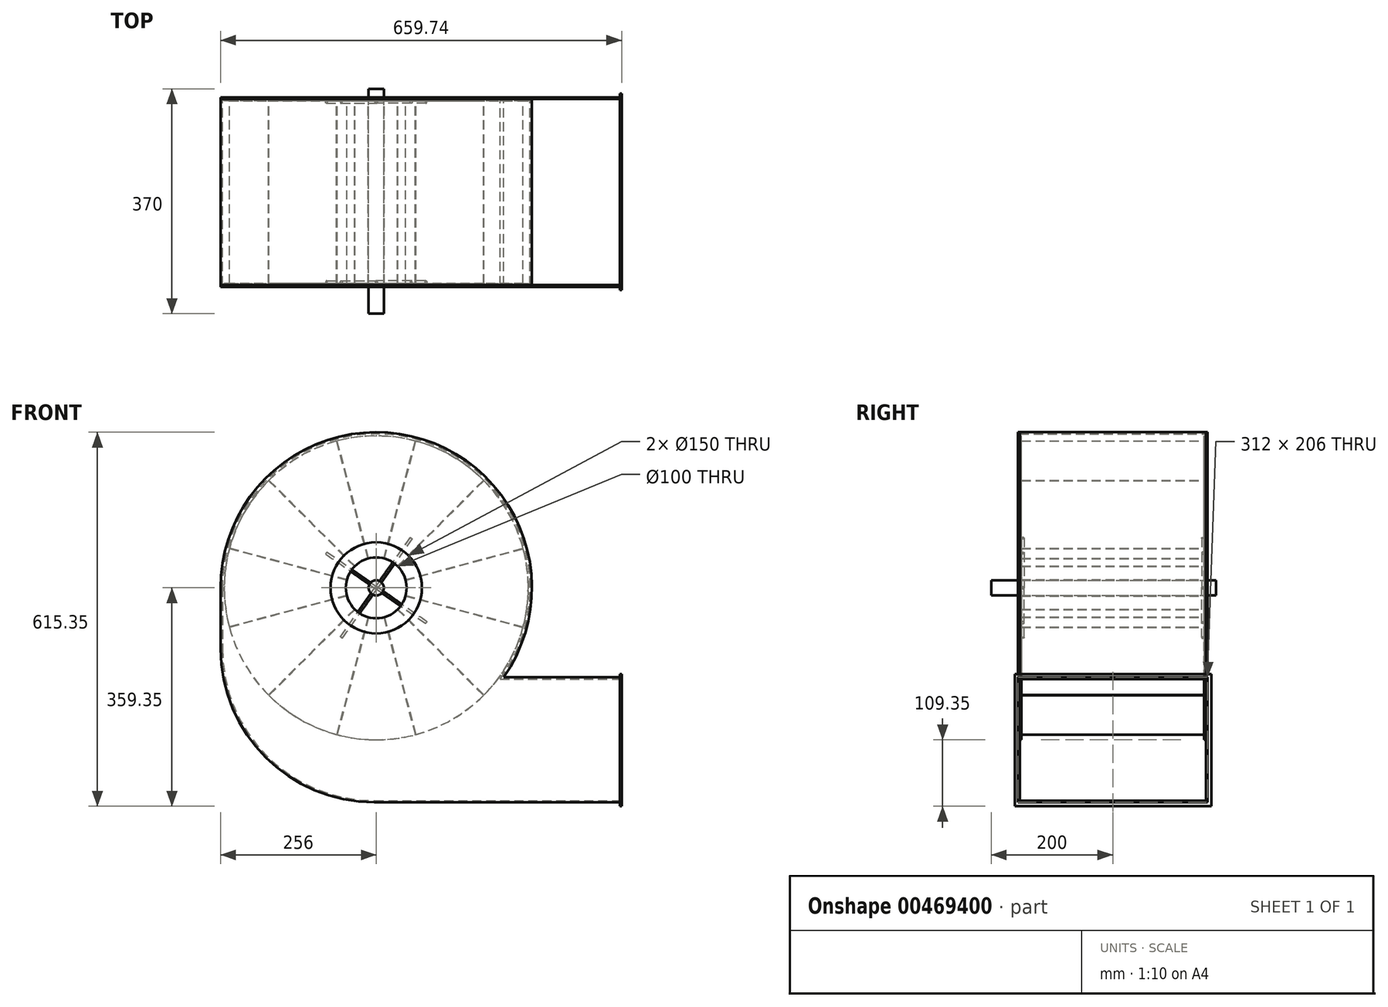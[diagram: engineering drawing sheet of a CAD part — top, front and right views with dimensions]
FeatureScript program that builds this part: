
annotation { "Feature Type Name" : "Feature", "Feature Type Description" : "" }
export const myFeature = defineFeature(function(context is Context, id is Id, definition is map)
    precondition{}
    {
        {
            var Q0;
            Q0=qCreatedBy(makeId("Front.planeOp"),FACE);
            var sketch = newSketch(context, id + "F0", { "sketchPlane" : qUnion([Q0])});
            skCircle(sketch, "E0", {"center": v(0, 0) * mm, "radius": 50 * mm});
            skCircle(sketch, "E1", {"center": v(0, 0) * mm, "radius": 250 * mm});
            skLineSegment(sketch, "E2", {"start": v(0, 0) * mm, "end": v(-176.78, 176.78) * mm, "construction": true});
            skLineSegment(sketch, "E3.0", {"start": v(-35, 35.7) * mm, "end": v(-176.42, 177.13) * mm});
            skLineSegment(sketch, "E4.0", {"start": v(-35.7, 35) * mm, "end": v(-177.13, 176.42) * mm});
            skLineSegment(sketch, "E5", {"start": v(-250, 0) * mm, "end": v(250, 0) * mm, "construction": true});
            skSolve(sketch);
        }
        {
            var Q0;
            {var subQ0=sQuery(id+"F0.wireOp",EDGE,"E3.0");Q0=makeQuery(id+"F0.imprint","IMPRINT",FACE,{"disambiguationData":[TD([[makeQuery(id+"F0.imprint","IMPRINT",EDGE,{"derivedFrom":subQ0}),-1.0]])]});}
            var Q1;
            {var subQ0=sQuery(id+"F0.wireOp",EDGE,"E3.0");Q1=makeQuery(id+"F0.imprint","IMPRINT",FACE,{"disambiguationData":[TD([[makeQuery(id+"F0.imprint","IMPRINT",EDGE,{"derivedFrom":subQ0}),1.0]])]});}
            extrude(context, id + "F1", {"entities" : qUnion([Q0, Q1]), "depth" : -3 * mm});
        }
        {
            var Q0;
            {var subQ0=sQuery(id+"F0.wireOp",EDGE,"E3.0");Q0=makeQuery(id+"F0.imprint","IMPRINT",FACE,{"disambiguationData":[TD([[makeQuery(id+"F0.imprint","IMPRINT",EDGE,{"derivedFrom":subQ0}),1.0]])]});}
            extrude(context, id + "F2", {"entities" : qUnion([Q0]), "depth" : 300 * mm});
        }
        {
            var Q0;
            Q0=makeQuery(id+"F2.opExtrude","SWEPT_BODY",BODY,{"disambiguationData":[OSD([sQuery(id+"F0.wireOp",EDGE,"E0"),sQuery(id+"F0.wireOp",EDGE,"E1"),sQuery(id+"F0.wireOp",EDGE,"E3.0"),sQuery(id+"F0.wireOp",EDGE,"E4.0")])]});
            var Q1;
            Q1=sQuery(id+"F0.wireOp",EDGE,"E1");
            circularPattern(context, id + "F3", {"entities" : qUnion([Q0]), "axis" : qUnion([Q1]), "angle" : 360 * degree, "instanceCount" : 12, "equalSpace" : true, "isCentered" : true});
        }
        {
            var Q0;
            Q0=makeQuery(id+"F1.opExtrude","SWEPT_BODY",BODY,{"disambiguationData":[OSD([sQuery(id+"F0.wireOp",EDGE,"E0"),sQuery(id+"F0.wireOp",EDGE,"E1"),sQuery(id+"F0.wireOp",EDGE,"E3.0"),sQuery(id+"F0.wireOp",EDGE,"E4.0")])]});
            var Q1;
            Q1=qCreatedBy(makeId("Front.planeOp"),FACE);
            transform(context, id + "F4", {"entities" : qUnion([Q0]), "transformType" : TransformType.TRANSLATION_DISTANCE, "transformDirection" : qUnion([Q1]), "distance" : 303 * mm, "makeCopy" : true});
        }
        {
            var Q0;
            Q0=qCreatedBy(makeId("Front.planeOp"),FACE);
            var sketch = newSketch(context, id + "F5", { "sketchPlane" : qUnion([Q0])});
            skCircle(sketch, "E6", {"center": v(0, 0) * mm, "radius": 12.5 * mm});
            skSolve(sketch);
        }
        {
            var Q0;
            Q0=makeQuery(id+"F5.imprint","IMPRINT",FACE,{"disambiguationData":[TD([[makeQuery(id+"F5.imprint","IMPRINT",EDGE,{"derivedFrom":sQuery(id+"F5.wireOp",EDGE,"E6")}),1.0]])]});
            extrude(context, id + "F6", {"entities" : qUnion([Q0]), "depth" : 350 * mm, "hasSecondDirection" : true, "secondDirectionOppositeDirection" : true, "secondDirectionDepth" : 20 * mm});
        }
        {
            var Q0;
            Q0=qCreatedBy(makeId("Front.planeOp"),FACE);
            var sketch = newSketch(context, id + "F7", { "sketchPlane" : qUnion([Q0])});
            skLineSegment(sketch, "E7", {"start": v(0, 0) * mm, "end": v(-81.92, 57.36) * mm});
            skLineSegment(sketch, "E8.0", {"start": v(1.15, 1.64) * mm, "end": v(-80.77, 59) * mm});
            skLineSegment(sketch, "E9", {"start": v(1.15, 1.64) * mm, "end": v(0, 0) * mm});
            skLineSegment(sketch, "E10", {"start": v(-80.77, 59) * mm, "end": v(-81.92, 57.36) * mm});
            skSolve(sketch);
        }
        {
            var Q0;
            Q0 = qSketchRegion(id + "F7", true);
            var Q1;
            Q1=sQuery(id+"F7.wireOp",EDGE,"E7");
            revolve(context, id + "F8", {"entities" : qUnion([Q0]), "axis" : qUnion([Q1]), "revolveType" : RevolveType.FULL});
        }
        {
            var Q0;
            Q0=makeQuery(id+"F8.opRevolve","SWEPT_BODY",BODY,{"disambiguationData":[OSD([sQuery(id+"F7.wireOp",EDGE,"E7"),sQuery(id+"F7.wireOp",EDGE,"E8.0"),sQuery(id+"F7.wireOp",EDGE,"E9"),sQuery(id+"F7.wireOp",EDGE,"E10")])]});
            var Q1;
            Q1=makeQuery(id+"F4.opPattern","COPY",EDGE,{"derivedFrom":makeQuery(id+"F1.opExtrude","CAP_EDGE",EDGE,{"disambiguationData":[OSD([sQuery(id+"F0.wireOp",EDGE,"E1")])],"isStart":true}),"instanceName":"1"});
            circularPattern(context, id + "F9", {"entities" : qUnion([Q0]), "axis" : qUnion([Q1]), "angle" : 360 * degree, "instanceCount" : 4, "equalSpace" : true});
        }
        {
            var Q0;
            Q0=makeQuery(id+"F8.opRevolve","SWEPT_BODY",BODY,{"disambiguationData":[OSD([sQuery(id+"F7.wireOp",EDGE,"E7"),sQuery(id+"F7.wireOp",EDGE,"E8.0"),sQuery(id+"F7.wireOp",EDGE,"E9"),sQuery(id+"F7.wireOp",EDGE,"E10")])]});
            var Q1;
            Q1=makeQuery(id+"F9.opPattern","COPY",BODY,{"derivedFrom":makeQuery(id+"F8.opRevolve","SWEPT_BODY",BODY,{"disambiguationData":[OSD([sQuery(id+"F7.wireOp",EDGE,"E7"),sQuery(id+"F7.wireOp",EDGE,"E8.0"),sQuery(id+"F7.wireOp",EDGE,"E9"),sQuery(id+"F7.wireOp",EDGE,"E10")])]}),"instanceName":"1"});
            var Q2;
            Q2=makeQuery(id+"F9.opPattern","COPY",BODY,{"derivedFrom":makeQuery(id+"F8.opRevolve","SWEPT_BODY",BODY,{"disambiguationData":[OSD([sQuery(id+"F7.wireOp",EDGE,"E7"),sQuery(id+"F7.wireOp",EDGE,"E8.0"),sQuery(id+"F7.wireOp",EDGE,"E9"),sQuery(id+"F7.wireOp",EDGE,"E10")])]}),"instanceName":"2"});
            var Q3;
            Q3=makeQuery(id+"F9.opPattern","COPY",BODY,{"derivedFrom":makeQuery(id+"F8.opRevolve","SWEPT_BODY",BODY,{"disambiguationData":[OSD([sQuery(id+"F7.wireOp",EDGE,"E7"),sQuery(id+"F7.wireOp",EDGE,"E8.0"),sQuery(id+"F7.wireOp",EDGE,"E9"),sQuery(id+"F7.wireOp",EDGE,"E10")])]}),"instanceName":"3"});
            var Q4;
            Q4=qCreatedBy(makeId("Front.planeOp"),FACE);
            transform(context, id + "F10", {"entities" : qUnion([Q0, Q1, Q2, Q3]), "transformType" : TransformType.TRANSLATION_DISTANCE, "transformDirection" : qUnion([Q4]), "distance" : 2 * mm, "makeCopy" : false});
        }
        {
            var Q0;
            Q0=qCreatedBy(makeId("Front.planeOp"),FACE);
            cPlane(context, id + "F11", {"entities" : qUnion([Q0]), "cplaneType" : CPlaneType.OFFSET, "offset" : (300 / 2) * mm, "width" : 152.4 * mm, "height" : 152.4 * mm});
        }
        {
            var Q0;
            Q0=makeQuery(id+"F9.opPattern","COPY",BODY,{"derivedFrom":makeQuery(id+"F8.opRevolve","SWEPT_BODY",BODY,{"disambiguationData":[OSD([sQuery(id+"F7.wireOp",EDGE,"E7"),sQuery(id+"F7.wireOp",EDGE,"E8.0"),sQuery(id+"F7.wireOp",EDGE,"E9"),sQuery(id+"F7.wireOp",EDGE,"E10")])]}),"instanceName":"3"});
            var Q1;
            Q1=makeQuery(id+"F8.opRevolve","SWEPT_BODY",BODY,{"disambiguationData":[OSD([sQuery(id+"F7.wireOp",EDGE,"E7"),sQuery(id+"F7.wireOp",EDGE,"E8.0"),sQuery(id+"F7.wireOp",EDGE,"E9"),sQuery(id+"F7.wireOp",EDGE,"E10")])]});
            var Q2;
            Q2=makeQuery(id+"F9.opPattern","COPY",BODY,{"derivedFrom":makeQuery(id+"F8.opRevolve","SWEPT_BODY",BODY,{"disambiguationData":[OSD([sQuery(id+"F7.wireOp",EDGE,"E7"),sQuery(id+"F7.wireOp",EDGE,"E8.0"),sQuery(id+"F7.wireOp",EDGE,"E9"),sQuery(id+"F7.wireOp",EDGE,"E10")])]}),"instanceName":"2"});
            var Q3;
            Q3=makeQuery(id+"F9.opPattern","COPY",BODY,{"derivedFrom":makeQuery(id+"F8.opRevolve","SWEPT_BODY",BODY,{"disambiguationData":[OSD([sQuery(id+"F7.wireOp",EDGE,"E7"),sQuery(id+"F7.wireOp",EDGE,"E8.0"),sQuery(id+"F7.wireOp",EDGE,"E9"),sQuery(id+"F7.wireOp",EDGE,"E10")])]}),"instanceName":"1"});
            var Q4;
            Q4=qCreatedBy(id+"F11.planeOp",FACE);
            mirror(context, id + "F12", {"entities" : qUnion([Q0, Q1, Q2, Q3]), "mirrorPlane" : qUnion([Q4])});
        }
        {
            var Q0;
            Q0=makeQuery(id+"F3.opPattern","COPY",BODY,{"derivedFrom":makeQuery(id+"F2.opExtrude","SWEPT_BODY",BODY,{"disambiguationData":[OSD([sQuery(id+"F0.wireOp",EDGE,"E0"),sQuery(id+"F0.wireOp",EDGE,"E1"),sQuery(id+"F0.wireOp",EDGE,"E3.0"),sQuery(id+"F0.wireOp",EDGE,"E4.0")])]}),"instanceName":"9"});
            var Q1;
            Q1=makeQuery(id+"F1.opExtrude","SWEPT_BODY",BODY,{"disambiguationData":[OSD([sQuery(id+"F0.wireOp",EDGE,"E0"),sQuery(id+"F0.wireOp",EDGE,"E1")])]});
            var Q2;
            Q2=makeQuery(id+"F2.opExtrude","SWEPT_BODY",BODY,{"disambiguationData":[OSD([sQuery(id+"F0.wireOp",EDGE,"E0"),sQuery(id+"F0.wireOp",EDGE,"E1"),sQuery(id+"F0.wireOp",EDGE,"E3.0"),sQuery(id+"F0.wireOp",EDGE,"E4.0")])]});
            var Q3;
            Q3=makeQuery(id+"F3.opPattern","COPY",BODY,{"derivedFrom":makeQuery(id+"F2.opExtrude","SWEPT_BODY",BODY,{"disambiguationData":[OSD([sQuery(id+"F0.wireOp",EDGE,"E0"),sQuery(id+"F0.wireOp",EDGE,"E1"),sQuery(id+"F0.wireOp",EDGE,"E3.0"),sQuery(id+"F0.wireOp",EDGE,"E4.0")])]}),"instanceName":"-11"});
            var Q4;
            Q4=makeQuery(id+"F3.opPattern","COPY",BODY,{"derivedFrom":makeQuery(id+"F2.opExtrude","SWEPT_BODY",BODY,{"disambiguationData":[OSD([sQuery(id+"F0.wireOp",EDGE,"E0"),sQuery(id+"F0.wireOp",EDGE,"E1"),sQuery(id+"F0.wireOp",EDGE,"E3.0"),sQuery(id+"F0.wireOp",EDGE,"E4.0")])]}),"instanceName":"-10"});
            var Q5;
            Q5=makeQuery(id+"F3.opPattern","COPY",BODY,{"derivedFrom":makeQuery(id+"F2.opExtrude","SWEPT_BODY",BODY,{"disambiguationData":[OSD([sQuery(id+"F0.wireOp",EDGE,"E0"),sQuery(id+"F0.wireOp",EDGE,"E1"),sQuery(id+"F0.wireOp",EDGE,"E3.0"),sQuery(id+"F0.wireOp",EDGE,"E4.0")])]}),"instanceName":"-9"});
            var Q6;
            Q6=makeQuery(id+"F3.opPattern","COPY",BODY,{"derivedFrom":makeQuery(id+"F2.opExtrude","SWEPT_BODY",BODY,{"disambiguationData":[OSD([sQuery(id+"F0.wireOp",EDGE,"E0"),sQuery(id+"F0.wireOp",EDGE,"E1"),sQuery(id+"F0.wireOp",EDGE,"E3.0"),sQuery(id+"F0.wireOp",EDGE,"E4.0")])]}),"instanceName":"-8"});
            var Q7;
            Q7=makeQuery(id+"F3.opPattern","COPY",BODY,{"derivedFrom":makeQuery(id+"F2.opExtrude","SWEPT_BODY",BODY,{"disambiguationData":[OSD([sQuery(id+"F0.wireOp",EDGE,"E0"),sQuery(id+"F0.wireOp",EDGE,"E1"),sQuery(id+"F0.wireOp",EDGE,"E3.0"),sQuery(id+"F0.wireOp",EDGE,"E4.0")])]}),"instanceName":"-7"});
            var Q8;
            Q8=makeQuery(id+"F3.opPattern","COPY",BODY,{"derivedFrom":makeQuery(id+"F2.opExtrude","SWEPT_BODY",BODY,{"disambiguationData":[OSD([sQuery(id+"F0.wireOp",EDGE,"E0"),sQuery(id+"F0.wireOp",EDGE,"E1"),sQuery(id+"F0.wireOp",EDGE,"E3.0"),sQuery(id+"F0.wireOp",EDGE,"E4.0")])]}),"instanceName":"-6"});
            var Q9;
            Q9=makeQuery(id+"F3.opPattern","COPY",BODY,{"derivedFrom":makeQuery(id+"F2.opExtrude","SWEPT_BODY",BODY,{"disambiguationData":[OSD([sQuery(id+"F0.wireOp",EDGE,"E0"),sQuery(id+"F0.wireOp",EDGE,"E1"),sQuery(id+"F0.wireOp",EDGE,"E3.0"),sQuery(id+"F0.wireOp",EDGE,"E4.0")])]}),"instanceName":"-5"});
            var Q10;
            Q10=makeQuery(id+"F3.opPattern","COPY",BODY,{"derivedFrom":makeQuery(id+"F2.opExtrude","SWEPT_BODY",BODY,{"disambiguationData":[OSD([sQuery(id+"F0.wireOp",EDGE,"E0"),sQuery(id+"F0.wireOp",EDGE,"E1"),sQuery(id+"F0.wireOp",EDGE,"E3.0"),sQuery(id+"F0.wireOp",EDGE,"E4.0")])]}),"instanceName":"-4"});
            var Q11;
            Q11=makeQuery(id+"F3.opPattern","COPY",BODY,{"derivedFrom":makeQuery(id+"F2.opExtrude","SWEPT_BODY",BODY,{"disambiguationData":[OSD([sQuery(id+"F0.wireOp",EDGE,"E0"),sQuery(id+"F0.wireOp",EDGE,"E1"),sQuery(id+"F0.wireOp",EDGE,"E3.0"),sQuery(id+"F0.wireOp",EDGE,"E4.0")])]}),"instanceName":"-3"});
            var Q12;
            Q12=makeQuery(id+"F3.opPattern","COPY",BODY,{"derivedFrom":makeQuery(id+"F2.opExtrude","SWEPT_BODY",BODY,{"disambiguationData":[OSD([sQuery(id+"F0.wireOp",EDGE,"E0"),sQuery(id+"F0.wireOp",EDGE,"E1"),sQuery(id+"F0.wireOp",EDGE,"E3.0"),sQuery(id+"F0.wireOp",EDGE,"E4.0")])]}),"instanceName":"-2"});
            var Q13;
            Q13=makeQuery(id+"F3.opPattern","COPY",BODY,{"derivedFrom":makeQuery(id+"F2.opExtrude","SWEPT_BODY",BODY,{"disambiguationData":[OSD([sQuery(id+"F0.wireOp",EDGE,"E0"),sQuery(id+"F0.wireOp",EDGE,"E1"),sQuery(id+"F0.wireOp",EDGE,"E3.0"),sQuery(id+"F0.wireOp",EDGE,"E4.0")])]}),"instanceName":"-1"});
            var Q14;
            Q14=makeQuery(id+"F3.opPattern","COPY",BODY,{"derivedFrom":makeQuery(id+"F2.opExtrude","SWEPT_BODY",BODY,{"disambiguationData":[OSD([sQuery(id+"F0.wireOp",EDGE,"E0"),sQuery(id+"F0.wireOp",EDGE,"E1"),sQuery(id+"F0.wireOp",EDGE,"E3.0"),sQuery(id+"F0.wireOp",EDGE,"E4.0")])]}),"instanceName":"1"});
            var Q15;
            Q15=makeQuery(id+"F3.opPattern","COPY",BODY,{"derivedFrom":makeQuery(id+"F2.opExtrude","SWEPT_BODY",BODY,{"disambiguationData":[OSD([sQuery(id+"F0.wireOp",EDGE,"E0"),sQuery(id+"F0.wireOp",EDGE,"E1"),sQuery(id+"F0.wireOp",EDGE,"E3.0"),sQuery(id+"F0.wireOp",EDGE,"E4.0")])]}),"instanceName":"2"});
            var Q16;
            Q16=makeQuery(id+"F3.opPattern","COPY",BODY,{"derivedFrom":makeQuery(id+"F2.opExtrude","SWEPT_BODY",BODY,{"disambiguationData":[OSD([sQuery(id+"F0.wireOp",EDGE,"E0"),sQuery(id+"F0.wireOp",EDGE,"E1"),sQuery(id+"F0.wireOp",EDGE,"E3.0"),sQuery(id+"F0.wireOp",EDGE,"E4.0")])]}),"instanceName":"3"});
            var Q17;
            Q17=makeQuery(id+"F3.opPattern","COPY",BODY,{"derivedFrom":makeQuery(id+"F2.opExtrude","SWEPT_BODY",BODY,{"disambiguationData":[OSD([sQuery(id+"F0.wireOp",EDGE,"E0"),sQuery(id+"F0.wireOp",EDGE,"E1"),sQuery(id+"F0.wireOp",EDGE,"E3.0"),sQuery(id+"F0.wireOp",EDGE,"E4.0")])]}),"instanceName":"4"});
            var Q18;
            Q18=makeQuery(id+"F3.opPattern","COPY",BODY,{"derivedFrom":makeQuery(id+"F2.opExtrude","SWEPT_BODY",BODY,{"disambiguationData":[OSD([sQuery(id+"F0.wireOp",EDGE,"E0"),sQuery(id+"F0.wireOp",EDGE,"E1"),sQuery(id+"F0.wireOp",EDGE,"E3.0"),sQuery(id+"F0.wireOp",EDGE,"E4.0")])]}),"instanceName":"5"});
            var Q19;
            Q19=makeQuery(id+"F3.opPattern","COPY",BODY,{"derivedFrom":makeQuery(id+"F2.opExtrude","SWEPT_BODY",BODY,{"disambiguationData":[OSD([sQuery(id+"F0.wireOp",EDGE,"E0"),sQuery(id+"F0.wireOp",EDGE,"E1"),sQuery(id+"F0.wireOp",EDGE,"E3.0"),sQuery(id+"F0.wireOp",EDGE,"E4.0")])]}),"instanceName":"6"});
            var Q20;
            Q20=makeQuery(id+"F3.opPattern","COPY",BODY,{"derivedFrom":makeQuery(id+"F2.opExtrude","SWEPT_BODY",BODY,{"disambiguationData":[OSD([sQuery(id+"F0.wireOp",EDGE,"E0"),sQuery(id+"F0.wireOp",EDGE,"E1"),sQuery(id+"F0.wireOp",EDGE,"E3.0"),sQuery(id+"F0.wireOp",EDGE,"E4.0")])]}),"instanceName":"7"});
            var Q21;
            Q21=makeQuery(id+"F3.opPattern","COPY",BODY,{"derivedFrom":makeQuery(id+"F2.opExtrude","SWEPT_BODY",BODY,{"disambiguationData":[OSD([sQuery(id+"F0.wireOp",EDGE,"E0"),sQuery(id+"F0.wireOp",EDGE,"E1"),sQuery(id+"F0.wireOp",EDGE,"E3.0"),sQuery(id+"F0.wireOp",EDGE,"E4.0")])]}),"instanceName":"8"});
            var Q22;
            Q22=makeQuery(id+"F3.opPattern","COPY",BODY,{"derivedFrom":makeQuery(id+"F2.opExtrude","SWEPT_BODY",BODY,{"disambiguationData":[OSD([sQuery(id+"F0.wireOp",EDGE,"E0"),sQuery(id+"F0.wireOp",EDGE,"E1"),sQuery(id+"F0.wireOp",EDGE,"E3.0"),sQuery(id+"F0.wireOp",EDGE,"E4.0")])]}),"instanceName":"10"});
            var Q23;
            Q23=makeQuery(id+"F3.opPattern","COPY",BODY,{"derivedFrom":makeQuery(id+"F2.opExtrude","SWEPT_BODY",BODY,{"disambiguationData":[OSD([sQuery(id+"F0.wireOp",EDGE,"E0"),sQuery(id+"F0.wireOp",EDGE,"E1"),sQuery(id+"F0.wireOp",EDGE,"E3.0"),sQuery(id+"F0.wireOp",EDGE,"E4.0")])]}),"instanceName":"11"});
            var Q24;
            Q24=makeQuery(id+"F4.opPattern","COPY",BODY,{"derivedFrom":makeQuery(id+"F1.opExtrude","SWEPT_BODY",BODY,{"disambiguationData":[OSD([sQuery(id+"F0.wireOp",EDGE,"E0"),sQuery(id+"F0.wireOp",EDGE,"E1")])]}),"instanceName":"1"});
            var Q25;
            Q25=makeQuery(id+"F8.opRevolve","SWEPT_BODY",BODY,{"disambiguationData":[OSD([sQuery(id+"F7.wireOp",EDGE,"E7"),sQuery(id+"F7.wireOp",EDGE,"E8.0"),sQuery(id+"F7.wireOp",EDGE,"E9"),sQuery(id+"F7.wireOp",EDGE,"E10")])]});
            booleanBodies(context, id + "F13", {"operationType" : BooleanOperationType.UNION, "tools" : qUnion([Q0, Q1, Q2, Q3, Q4, Q5, Q6, Q7, Q8, Q9, Q10, Q11, Q12, Q13, Q14, Q15, Q16, Q17, Q18, Q19, Q20, Q21, Q22, Q23, Q24, Q25])});
        }
        {
            var Q0;
            Q0=qCreatedBy(id+"F11.planeOp",FACE);
            var sketch = newSketch(context, id + "F14", { "sketchPlane" : qUnion([Q0])});
            skArc(sketch, "E11", {"start": v(203.74, -150) * mm, "mid": v(78.94, 240.37) * mm, "end": v(-253, 0) * mm});
            skLineSegment(sketch, "E12", {"start": v(-253, 0) * mm, "end": v(-253, -100) * mm});
            skLineSegment(sketch, "E13", {"start": v(-3, -350) * mm, "end": v(403.74, -350) * mm});
            skLineSegment(sketch, "E14", {"start": v(203.74, -150) * mm, "end": v(403.74, -150) * mm});
            skPoint(sketch, "E15.visualSharp", {"position": v(-253, -350) * mm});
            skArc(sketch, "E16", {"start": v(-3, -350) * mm, "mid": v(-179.78, -276.78) * mm, "end": v(-253, -100) * mm});
            skArc(sketch, "E17.0", {"start": v(209.59, -147) * mm, "mid": v(77.08, 244.12) * mm, "end": v(-256, 0) * mm});
            skArc(sketch, "E17.1", {"start": v(-3, -353) * mm, "mid": v(-181.9, -278.9) * mm, "end": v(-256, -100) * mm});
            skLineSegment(sketch, "E17.2", {"start": v(-3, -353) * mm, "end": v(403.74, -353) * mm});
            skLineSegment(sketch, "E17.3", {"start": v(-256, 0) * mm, "end": v(-256, -100) * mm});
            skLineSegment(sketch, "E17.5", {"start": v(209.59, -147) * mm, "end": v(403.74, -147) * mm});
            skLineSegment(sketch, "E18", {"start": v(403.74, -147) * mm, "end": v(403.74, -150) * mm});
            skLineSegment(sketch, "E19", {"start": v(403.74, -350) * mm, "end": v(403.74, -353) * mm});
            skSolve(sketch);
        }
        {
            var Q0;
            Q0 = qSketchRegion(id + "F14", true);
            extrude(context, id + "F15", {"entities" : qUnion([Q0]), "endBound" : BoundingType.SYMMETRIC, "depth" : 306 * mm});
        }
        {
            var Q0;
            Q0=makeQuery(id+"F15.opExtrude","CAP_FACE",FACE,{"disambiguationData":[OSD([sQuery(id+"F14.wireOp",EDGE,"E11"),sQuery(id+"F14.wireOp",EDGE,"E12"),sQuery(id+"F14.wireOp",EDGE,"E13"),sQuery(id+"F14.wireOp",EDGE,"E14"),sQuery(id+"F14.wireOp",EDGE,"E16"),sQuery(id+"F14.wireOp",EDGE,"E17.0"),sQuery(id+"F14.wireOp",EDGE,"E17.1"),sQuery(id+"F14.wireOp",EDGE,"E17.2"),sQuery(id+"F14.wireOp",EDGE,"E17.3"),sQuery(id+"F14.wireOp",EDGE,"E17.5"),sQuery(id+"F14.wireOp",EDGE,"E18"),sQuery(id+"F14.wireOp",EDGE,"E19")])],"isStart":false});
            var sketch = newSketch(context, id + "F16", { "sketchPlane" : qUnion([Q0])});
            skArc(sketch, "E20.0", {"start": v(209.59, -147) * mm, "mid": v(77.08, 244.12) * mm, "end": v(-256, 0) * mm});
            skLineSegment(sketch, "E20.1", {"start": v(209.59, -147) * mm, "end": v(403.74, -147) * mm});
            skArc(sketch, "E20.2", {"start": v(-3, -353) * mm, "mid": v(-181.9, -278.9) * mm, "end": v(-256, -100) * mm});
            skLineSegment(sketch, "E20.3", {"start": v(-3, -353) * mm, "end": v(403.74, -353) * mm});
            skLineSegment(sketch, "E20.4", {"start": v(-256, 0) * mm, "end": v(-256, -100) * mm});
            skLineSegment(sketch, "E21", {"start": v(403.74, -147) * mm, "end": v(403.74, -353) * mm});
            skCircle(sketch, "E22", {"center": v(0, 0) * mm, "radius": 75 * mm});
            skPoint(sketch, "E22.first.point", {"position": v(74.67, -7.07) * mm});
            skPoint(sketch, "E22.second.point", {"position": v(-48.8, 56.95) * mm});
            skPoint(sketch, "E22.third.point", {"position": v(45.4, 59.7) * mm});
            skSolve(sketch);
        }
        {
            var Q0;
            Q0 = qSketchRegion(id + "F16", true);
            extrude(context, id + "F17", {"entities" : qUnion([Q0]), "depth" : 3 * mm});
        }
        {
            var Q0;
            Q0=makeQuery(id+"F17.opExtrude","SWEPT_BODY",BODY,{"disambiguationData":[OSD([sQuery(id+"F16.wireOp",EDGE,"E20.0"),sQuery(id+"F16.wireOp",EDGE,"E20.1"),sQuery(id+"F16.wireOp",EDGE,"E20.2"),sQuery(id+"F16.wireOp",EDGE,"E20.3"),sQuery(id+"F16.wireOp",EDGE,"E20.4"),sQuery(id+"F16.wireOp",EDGE,"E21")])]});
            var Q1;
            Q1=qCreatedBy(id+"F11.planeOp",FACE);
            mirror(context, id + "F18", {"entities" : qUnion([Q0]), "mirrorPlane" : qUnion([Q1])});
        }
        {
            var Q0;
            Q0=makeQuery(id+"F17.opExtrude","SWEPT_FACE",FACE,{"disambiguationData":[OSD([sQuery(id+"F16.wireOp",EDGE,"E21")])]});
            var sketch = newSketch(context, id + "F19", { "sketchPlane" : qUnion([Q0])});
            skLineSegment(sketch, "E23.0", {"start": v(-306, -147) * mm, "end": v(-306, -353.88) * mm});
            skLineSegment(sketch, "E24.0", {"start": v(-306, -147) * mm, "end": v(6, -147) * mm});
            skLineSegment(sketch, "E25.0", {"start": v(6, -147) * mm, "end": v(6, -353) * mm});
            skLineSegment(sketch, "E26.0", {"start": v(-306, -353) * mm, "end": v(6, -353) * mm});
            skPoint(sketch, "E27.orphan", {"position": v(-306, -353) * mm});
            skLineSegment(sketch, "E28.0", {"start": v(-311, -142) * mm, "end": v(-311, -359.35) * mm});
            skLineSegment(sketch, "E28.1", {"start": v(-311, -142) * mm, "end": v(12.35, -142) * mm});
            skLineSegment(sketch, "E29.0", {"start": v(12.35, -142) * mm, "end": v(12.35, -359.35) * mm});
            skLineSegment(sketch, "E29.1", {"start": v(-311, -359.35) * mm, "end": v(12.35, -359.35) * mm});
            skSolve(sketch);
        }
        {
            var Q0;
            Q0 = qSketchRegion(id + "F19", true);
            extrude(context, id + "F20", {"entities" : qUnion([Q0]), "oppositeDirection" : true, "depth" : 3 * mm});
        }
    });
